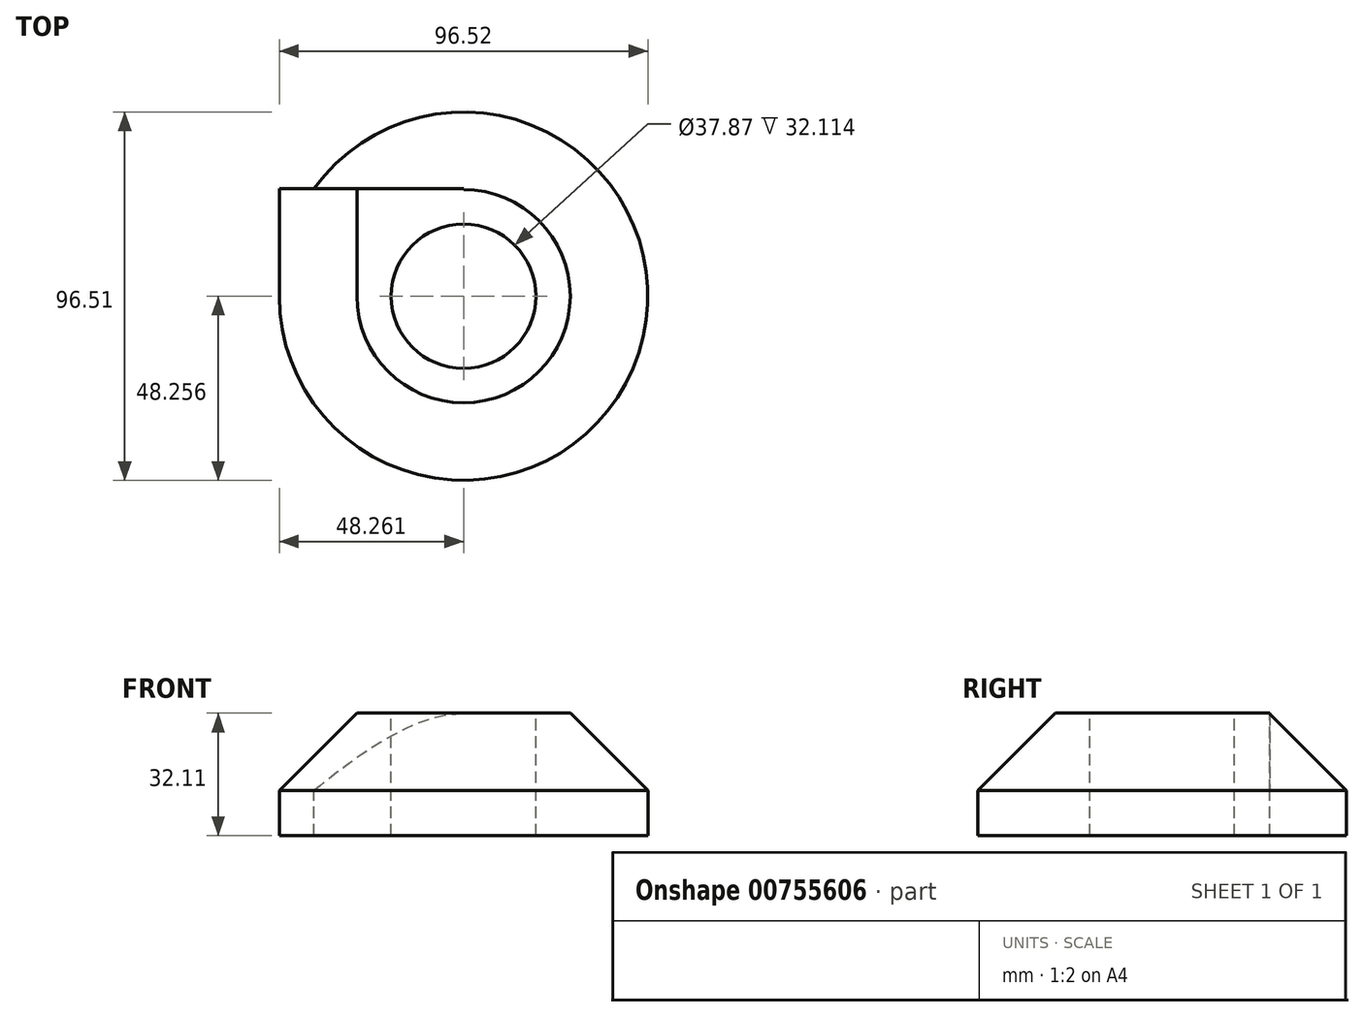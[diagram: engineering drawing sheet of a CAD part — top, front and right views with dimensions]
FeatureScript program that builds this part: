
annotation { "Feature Type Name" : "Feature", "Feature Type Description" : "" }
export const myFeature = defineFeature(function(context is Context, id is Id, definition is map)
    precondition{}
    {
        {
            var Q0;
            Q0=qCreatedBy(makeId("Front.planeOp"),FACE);
            var sketch = newSketch(context, id + "F0", { "sketchPlane" : qUnion([Q0])});
            skLineSegment(sketch, "E0.bottom", {"start": v(-59.19, 39.31) * mm, "end": v(18.6, 39.31) * mm});
            skLineSegment(sketch, "E0.top", {"start": v(-59.19, -8.86) * mm, "end": v(18.6, -8.86) * mm});
            skLineSegment(sketch, "E0.left", {"start": v(-59.19, 39.31) * mm, "end": v(-59.19, -8.86) * mm});
            skLineSegment(sketch, "E0.right", {"start": v(18.6, 39.31) * mm, "end": v(18.6, -8.86) * mm});
            skLineSegment(sketch, "E1.bottom", {"start": v(-59.19, -8.86) * mm, "end": v(-107.45, -8.86) * mm});
            skLineSegment(sketch, "E1.top", {"start": v(-59.19, 23.25) * mm, "end": v(-107.45, 23.25) * mm});
            skLineSegment(sketch, "E1.left", {"start": v(-59.19, -8.86) * mm, "end": v(-59.19, 23.25) * mm});
            skLineSegment(sketch, "E1.right", {"start": v(-107.45, -8.86) * mm, "end": v(-107.45, 23.25) * mm});
            skSolve(sketch);
        }
        {
            var Q0;
            {var subQ0=sQuery(id+"F0.wireOp",EDGE,"E1.bottom");Q0=makeQuery(id+"F0.imprint","IMPRINT",FACE,{"disambiguationData":[TD([[makeQuery(id+"F0.imprint","IMPRINT",EDGE,{"derivedFrom":subQ0}),-1.0]])]});}
            extrude(context, id + "F1", {"entities" : qUnion([Q0]), "depth" : 28.2 * mm, "offsetDistance" : 25.4 * mm});
        }
        {
            var Q0;
            Q0=makeQuery(id+"F1.opExtrude","SWEPT_EDGE",EDGE,{"disambiguationData":[OSD([sQuery(id+"F0.wireOp",EDGE,"E1.top"),sQuery(id+"F0.wireOp",EDGE,"E1.right")])]});
            chamfer(context, id + "F2", {"entities" : qUnion([Q0]), "width" : 20.32 * mm, "tangentPropagation" : true});
        }
        {
            var Q0;
            Q0=makeQuery(id+"F1.opExtrude","CAP_FACE",FACE,{"disambiguationData":[OSD([sQuery(id+"F0.wireOp",EDGE,"E0.left"),sQuery(id+"F0.wireOp",EDGE,"E1.bottom"),sQuery(id+"F0.wireOp",EDGE,"E1.top"),sQuery(id+"F0.wireOp",EDGE,"E1.right")])],"isStart":false});
            var Q1;
            Q1=makeQuery(id+"F1.opExtrude","CAP_EDGE",EDGE,{"disambiguationData":[OSD([sQuery(id+"F0.wireOp",EDGE,"E0.left")])],"isStart":false});
            revolve(context, id + "F3", {"operationType" : NewBodyOperationType.ADD, "surfaceOperationType" : NewSurfaceOperationType.NEW, "entities" : qUnion([Q0]), "axis" : qUnion([Q1]), "revolveType" : RevolveType.FULL});
        }
        {
            var Q0;
            {var subQ0=sQuery(id+"F0.wireOp",EDGE,"E1.top");Q0=makeQuery(id+"F3.boolean.opBoolean","MERGE",FACE,{"derivedFrom":[makeQuery(id+"F1.opExtrude","SWEPT_FACE",FACE,{"disambiguationData":[OSD([subQ0])]}),makeQuery(id+"F3.opRevolve","SWEPT_FACE",FACE,{"disambiguationData":[OSD([subQ0])]})]});}
            var sketch = newSketch(context, id + "F4", { "sketchPlane" : qUnion([Q0])});
            skCircle(sketch, "E2", {"center": v(-59.19, -28.2) * mm, "radius": 18.93 * mm});
            skSolve(sketch);
        }
        {
            var Q0;
            Q0=makeQuery(id+"F4.imprint","IMPRINT",FACE,{"disambiguationData":[TD([[makeQuery(id+"F4.imprint","IMPRINT",EDGE,{"derivedFrom":sQuery(id+"F4.wireOp",EDGE,"E2")}),1.0]])]});
            extrude(context, id + "F5", {"entities" : qUnion([Q0]), "operationType" : NewBodyOperationType.REMOVE, "endBound" : BoundingType.UP_TO_NEXT, "oppositeDirection" : true, "depth" : 122.43 * mm, "offsetDistance" : 25.4 * mm});
        }
    });
